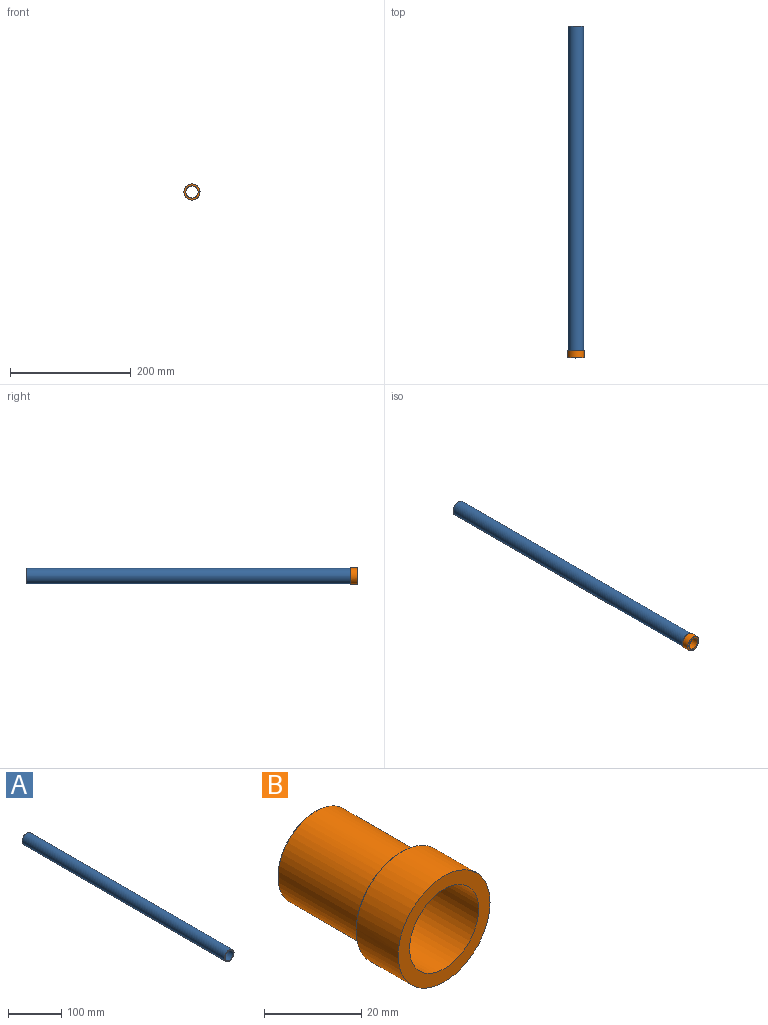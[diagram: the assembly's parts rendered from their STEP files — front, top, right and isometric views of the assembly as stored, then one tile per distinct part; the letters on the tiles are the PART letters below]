
ASSEMBLY  parts=2 mates=1
PART A: 4 faces, bbox 25.4x538.2x25.4 mm
  f0: cylinder r=11.08mm len=538.16mm, axis (0,1,0), area 37465.6mm2, adj f2,f3
  f1: cylinder r=12.7mm len=538.16mm, axis (0,1,0), area 42943.5mm2, adj f2,f3
  f2: plane 25.4x25.4mm, normal (0,-1,0), area 121mm2, adj f0,f1
  f3: plane 25.4x25.4mm, normal (0,1,0), area 121mm2, adj f0,f1
PART B: 8 faces, bbox 26.7x37.5x26.7 mm
  f0: cylinder r=10.05mm len=37.5mm, axis (0,1,0), area 2368mm2, adj f2,f5
  f1: cylinder r=13.35mm len=26.7mm, axis (0,1,0), area 1027.5mm2, adj f2,f7
  f2: plane 26.7x26.7mm, normal (0,-1,0), area 242.6mm2, adj f0,f1
  f3: plane 26.2x26.2mm, normal (0,1,0), area 153.4mm2, adj f4,f7
  f4: cylinder r=11.08mm len=24.75mm, axis (0,-1,0), area 1723mm2, adj f3,f6
  f5: plane 21.66x21.66mm, normal (0,1,0), area 51.2mm2, adj f0,f6
  f6: cone r=10.83mm half-angle=45deg, axis (0,-1,0), area 24.3mm2, adj f4,f5
  f7: cone r=13.35mm half-angle=45deg, axis (0,-1,0), area 29.4mm2, adj f1,f3
PLACE A t=(-142.92,107.53,-109.18)mm
PLACE B t=(-142.92,-161.56,-109.18)mm
MATE fastened A.f0 <-> B.f0  axis (0,1,0) through (-142.92,-161.56,-109.18)mm
